# Revit family: EVS
name_source: partatom
category: Lighting Fixtures
units: mm (PartAtom-declared; Revit-internal decimal feet)

## family parameters
Cut with Voids When Loaded = No
Host = Face
Light Source = Yes
OmniClass Number = 23.80.70.11.14.17
OmniClass Title = Direct/Indirect
Part Type = Normal
Room Calculation Point = No
Round Connector Dimension = Use Diameter
Shared = Yes

## types (1)
- EVS
    Apparent Load = 30 VA
    Assembly Code = D5020200
    Color Filter = 16777215
    Connector Description = Lighting Connector
    Default Elevation = 48 "
    Description = The EVS is specifically designed for general illumination in residential and commercial applications for indoor/outdoor protected environments
    Dimming Lamp Color Temperature Shift = <None>
    Emit Shape Visible in Rendering = No
    Emit from Circle Diameter = 8.5 "
    Features = Offered in AC only, AC and Emergency, with Heater Option
• Includes Self-Test , Self-Diagnostics
• 1200 Lumens in AC normally-On, and 350 Lumens in
Emergency
• 4000K color temperature
• LED life-cycle of 50,000 hours
• Dual-voltage 120 or 277 VAC input, 50/60Hz.
• Emergency models designed for 90 minute runtime
• AC and Heater Option Models:-30°C to 40°C(-22°F to 104°F)
• Emergency Models: 0°C to 40°C(32°F to 104°F)
    Fixture distribution = Direct
    Glass = Glass
    Housing Material = Paint -Brushed Nickel
    Lamp = LED
    Load Classification = Lighting
    Manufacturer = Dual Light
    Model = EVS Series
    Photometric Web File = EVS_20.00971 AC.ies
    Power Factor = 1
    Tilt Angle = -90°
    URL = https://www.currentlighting.com
    Voltage = 120 V
    Warranty = 5 year Warranty
    Wattage Comments = 30W
    Watts = 30 W

## geometry (parser evidence)
native form markers: Sweep x2
no freeform markers — native parametric forms only
